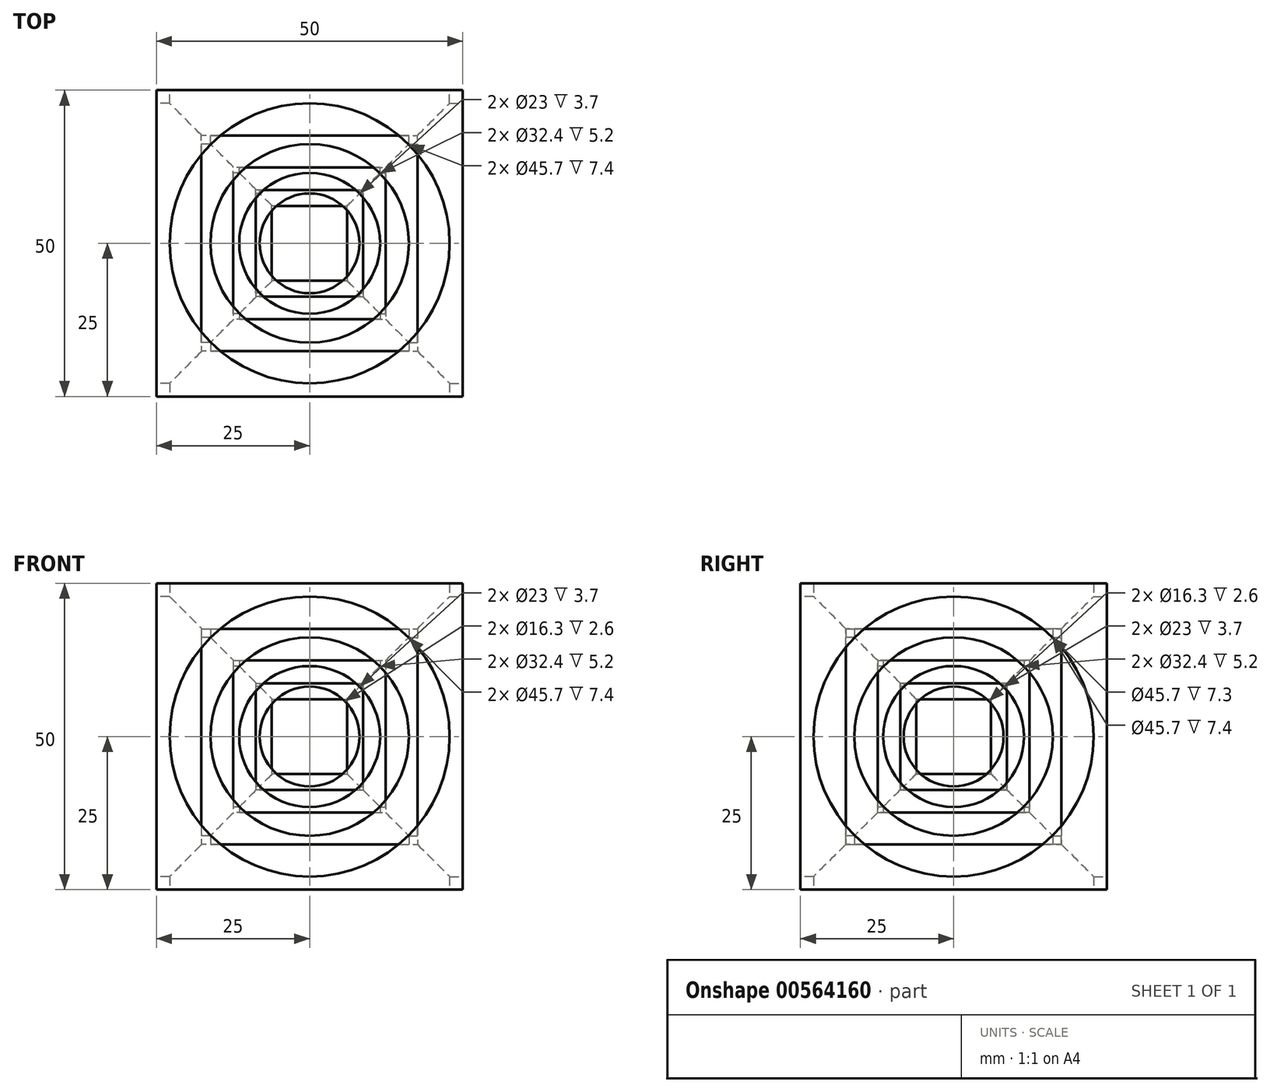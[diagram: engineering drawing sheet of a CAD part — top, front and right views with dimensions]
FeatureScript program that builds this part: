
annotation { "Feature Type Name" : "Feature", "Feature Type Description" : "" }
export const myFeature = defineFeature(function(context is Context, id is Id, definition is map)
    precondition{}
    {
        {
            assignVariable(context, id + "F0", {"name" : "S0", "anyValue" : 50});
        }
        {
            var Q0;
            Q0=qCreatedBy(makeId("Front.planeOp"),FACE);
            var sketch = newSketch(context, id + "F1", { "sketchPlane" : qUnion([Q0])});
            skLineSegment(sketch, "E0", {"start": v(0, 0) * mm, "end": v(-25, 0) * mm, "construction": true});
            skLineSegment(sketch, "E1", {"start": v(-25, 0) * mm, "end": v(-25, 25) * mm});
            skLineSegment(sketch, "E2", {"start": v(-25, 25) * mm, "end": v(25, 25) * mm});
            skLineSegment(sketch, "E3", {"start": v(-25, 0) * mm, "end": v(-25, -25) * mm});
            skLineSegment(sketch, "E4", {"start": v(-25, -25) * mm, "end": v(25, -25) * mm});
            skLineSegment(sketch, "E5", {"start": v(25, -25) * mm, "end": v(25, 25) * mm});
            skSolve(sketch);
        }
        {
            var Q0;
            Q0 = qSketchRegion(id + "F1", true);
            extrude(context, id + "F2", {"entities" : qUnion([Q0]), "depth" : getVariable(context, 'S0') * mm, "offsetDistance" : 25 * mm, "symmetric" : true});
        }
        {
            var Q0;
            Q0=qCreatedBy(makeId("Front.planeOp"),FACE);
            var sketch = newSketch(context, id + "F3", { "sketchPlane" : qUnion([Q0])});
            skLineSegment(sketch, "E6.0.0", {"start": v(-25, -25) * mm, "end": v(25, -25) * mm, "construction": true});
            skLineSegment(sketch, "E6.0.1", {"start": v(25, -25) * mm, "end": v(25, 25) * mm, "construction": true});
            skLineSegment(sketch, "E6.0.2", {"start": v(25, 25) * mm, "end": v(-25, 25) * mm, "construction": true});
            skLineSegment(sketch, "E6.0.3", {"start": v(-25, 25) * mm, "end": v(-25, -25) * mm, "construction": true});
            skLineSegment(sketch, "E7", {"start": v(0, 25) * mm, "end": v(0, 17.6) * mm, "construction": true});
            skPoint(sketch, "E7.endSnap0", {"position": v(0, 25) * mm});
            skLineSegment(sketch, "E8", {"start": v(0, 17.6) * mm, "end": v(0, 12.4) * mm, "construction": true});
            skLineSegment(sketch, "E9", {"start": v(0, 12.4) * mm, "end": v(0, 8.7) * mm, "construction": true});
            skLineSegment(sketch, "E10", {"start": v(0, 8.7) * mm, "end": v(0, 6.1) * mm, "construction": true});
            skLineSegment(sketch, "E11", {"start": v(0, 17.6) * mm, "end": v(22.85, 17.6) * mm, "construction": true});
            skLineSegment(sketch, "E12", {"start": v(0, 12.4) * mm, "end": v(16.2, 12.4) * mm, "construction": true});
            skLineSegment(sketch, "E13", {"start": v(0, 8.7) * mm, "end": v(11.5, 8.7) * mm, "construction": true});
            skLineSegment(sketch, "E14", {"start": v(0, 6.1) * mm, "end": v(8.15, 6.1) * mm, "construction": true});
            skLineSegment(sketch, "E15", {"start": v(0, 25) * mm, "end": v(22.85, 25) * mm});
            skLineSegment(sketch, "E16", {"start": v(22.85, 25) * mm, "end": v(22.85, 17.6) * mm});
            skLineSegment(sketch, "E17", {"start": v(22.85, 17.6) * mm, "end": v(16.2, 17.6) * mm});
            skLineSegment(sketch, "E18", {"start": v(16.2, 17.6) * mm, "end": v(16.2, 12.4) * mm});
            skLineSegment(sketch, "E19", {"start": v(16.2, 12.4) * mm, "end": v(11.5, 12.4) * mm});
            skLineSegment(sketch, "E20", {"start": v(11.5, 12.4) * mm, "end": v(11.5, 8.7) * mm});
            skLineSegment(sketch, "E21", {"start": v(8.15, 8.7) * mm, "end": v(11.5, 8.7) * mm});
            skLineSegment(sketch, "E22", {"start": v(8.15, 8.7) * mm, "end": v(8.15, 6.1) * mm});
            skLineSegment(sketch, "E23", {"start": v(0, 6.1) * mm, "end": v(0, 25) * mm});
            skLineSegment(sketch, "E24", {"start": v(8.15, 6.1) * mm, "end": v(0, 6.1) * mm});
            skSolve(sketch);
        }
        {
            var Q0;
            Q0 = qSketchRegion(id + "F3", true);
            var Q1;
            Q1=sQuery(id+"F3.wireOp",EDGE,"E23");
            revolve(context, id + "F4", {"operationType" : NewBodyOperationType.REMOVE, "entities" : qUnion([Q0]), "axis" : qUnion([Q1]), "revolveType" : RevolveType.FULL});
        }
        {
            var Q0;
            Q0=qCreatedBy(makeId("Front.planeOp"),FACE);
            var sketch = newSketch(context, id + "F5", { "sketchPlane" : qUnion([Q0])});
            skPoint(sketch, "E25.0", {"position": v(25, 25) * mm});
            skPoint(sketch, "E26.0", {"position": v(-25, 25) * mm});
            skPoint(sketch, "E27.0", {"position": v(-25, -25) * mm});
            skPoint(sketch, "E28.0", {"position": v(25, -25) * mm});
            skLineSegment(sketch, "E29.0.0", {"start": v(25, 25) * mm, "end": v(-25, 25) * mm, "construction": true});
            skLineSegment(sketch, "E29.0.1", {"start": v(-25, 25) * mm, "end": v(-25, -25) * mm, "construction": true});
            skLineSegment(sketch, "E29.0.2", {"start": v(-25, -25) * mm, "end": v(25, -25) * mm, "construction": true});
            skLineSegment(sketch, "E29.0.3", {"start": v(25, -25) * mm, "end": v(25, 25) * mm, "construction": true});
            skLineSegment(sketch, "E30", {"start": v(0, -25) * mm, "end": v(0, -17.6) * mm, "construction": true});
            skPoint(sketch, "E30.endSnap0", {"position": v(0, -25) * mm});
            skLineSegment(sketch, "E31", {"start": v(0, -17.6) * mm, "end": v(0, -12.4) * mm, "construction": true});
            skLineSegment(sketch, "E32", {"start": v(0, -12.4) * mm, "end": v(0, -8.7) * mm, "construction": true});
            skLineSegment(sketch, "E33", {"start": v(0, -8.7) * mm, "end": v(0, -6.1) * mm, "construction": true});
            skLineSegment(sketch, "E34", {"start": v(0, -17.6) * mm, "end": v(-22.85, -17.6) * mm, "construction": true});
            skLineSegment(sketch, "E35", {"start": v(0, -12.4) * mm, "end": v(-16.2, -12.4) * mm, "construction": true});
            skLineSegment(sketch, "E36", {"start": v(0, -8.7) * mm, "end": v(-11.5, -8.7) * mm, "construction": true});
            skLineSegment(sketch, "E37", {"start": v(0, -6.1) * mm, "end": v(-8.15, -6.1) * mm, "construction": true});
            skLineSegment(sketch, "E38", {"start": v(0, -25) * mm, "end": v(-22.85, -25) * mm});
            skLineSegment(sketch, "E39", {"start": v(-22.85, -25) * mm, "end": v(-22.85, -17.6) * mm});
            skLineSegment(sketch, "E40", {"start": v(-22.85, -17.6) * mm, "end": v(-16.2, -17.6) * mm});
            skLineSegment(sketch, "E41", {"start": v(-16.2, -17.6) * mm, "end": v(-16.2, -12.4) * mm});
            skLineSegment(sketch, "E42", {"start": v(-16.2, -12.4) * mm, "end": v(-11.5, -12.4) * mm});
            skLineSegment(sketch, "E43", {"start": v(-11.5, -12.4) * mm, "end": v(-11.5, -8.7) * mm});
            skLineSegment(sketch, "E44", {"start": v(-8.15, -8.7) * mm, "end": v(-11.5, -8.7) * mm});
            skLineSegment(sketch, "E45", {"start": v(-8.15, -8.7) * mm, "end": v(-8.15, -6.1) * mm});
            skLineSegment(sketch, "E46", {"start": v(0, -6.1) * mm, "end": v(0, -25) * mm});
            skLineSegment(sketch, "E47", {"start": v(-8.15, -6.1) * mm, "end": v(0, -6.1) * mm});
            skSolve(sketch);
        }
        {
            var Q0;
            Q0 = qSketchRegion(id + "F5", true);
            var Q1;
            Q1=sQuery(id+"F5.wireOp",EDGE,"E46");
            revolve(context, id + "F6", {"operationType" : NewBodyOperationType.REMOVE, "entities" : qUnion([Q0]), "axis" : qUnion([Q1]), "revolveType" : RevolveType.FULL, "oppositeDirection" : true});
        }
        {
            var Q0;
            Q0=qCreatedBy(makeId("Right.planeOp"),FACE);
            var sketch = newSketch(context, id + "F7", { "sketchPlane" : qUnion([Q0])});
            skPoint(sketch, "E48.0", {"position": v(-25, 25) * mm});
            skPoint(sketch, "E49.0", {"position": v(25, -25) * mm});
            skPoint(sketch, "E50.0", {"position": v(25, 25) * mm});
            skPoint(sketch, "E51.0", {"position": v(-25, -25) * mm});
            skLineSegment(sketch, "E52.0.0", {"start": v(25, -25) * mm, "end": v(25, 25) * mm, "construction": true});
            skLineSegment(sketch, "E52.0.1", {"start": v(25, 25) * mm, "end": v(-25, 25) * mm, "construction": true});
            skLineSegment(sketch, "E52.0.2", {"start": v(-25, 25) * mm, "end": v(-25, -25) * mm, "construction": true});
            skLineSegment(sketch, "E52.0.3", {"start": v(-25, -25) * mm, "end": v(25, -25) * mm, "construction": true});
            skLineSegment(sketch, "E53", {"start": v(-25, 0) * mm, "end": v(-17.6, 0) * mm, "construction": true});
            skPoint(sketch, "E53.endSnap0", {"position": v(-25, 0) * mm});
            skLineSegment(sketch, "E54", {"start": v(-17.6, 0) * mm, "end": v(-12.4, 0) * mm, "construction": true});
            skLineSegment(sketch, "E55", {"start": v(-12.4, 0) * mm, "end": v(-8.7, 0) * mm, "construction": true});
            skLineSegment(sketch, "E56", {"start": v(-8.7, 0) * mm, "end": v(-6.1, 0) * mm, "construction": true});
            skLineSegment(sketch, "E57", {"start": v(-17.6, 0) * mm, "end": v(-17.6, 22.85) * mm, "construction": true});
            skLineSegment(sketch, "E58", {"start": v(-12.4, 0) * mm, "end": v(-12.4, 16.2) * mm, "construction": true});
            skLineSegment(sketch, "E59", {"start": v(-8.7, 0) * mm, "end": v(-8.7, 11.5) * mm, "construction": true});
            skLineSegment(sketch, "E60", {"start": v(-6.1, 0) * mm, "end": v(-6.1, 8.15) * mm, "construction": true});
            skLineSegment(sketch, "E61", {"start": v(-25, 0) * mm, "end": v(-25, 22.85) * mm});
            skLineSegment(sketch, "E62", {"start": v(-25, 22.85) * mm, "end": v(-17.6, 22.85) * mm});
            skLineSegment(sketch, "E63", {"start": v(-17.6, 22.85) * mm, "end": v(-17.6, 16.2) * mm});
            skLineSegment(sketch, "E64", {"start": v(-17.6, 16.2) * mm, "end": v(-12.4, 16.2) * mm});
            skLineSegment(sketch, "E65", {"start": v(-12.4, 16.2) * mm, "end": v(-12.4, 11.5) * mm});
            skLineSegment(sketch, "E66", {"start": v(-12.4, 11.5) * mm, "end": v(-8.7, 11.5) * mm});
            skLineSegment(sketch, "E67", {"start": v(-8.7, 8.15) * mm, "end": v(-8.7, 11.5) * mm});
            skLineSegment(sketch, "E68", {"start": v(-8.7, 8.15) * mm, "end": v(-6.1, 8.15) * mm});
            skLineSegment(sketch, "E69", {"start": v(-6.1, 0) * mm, "end": v(-25, 0) * mm});
            skLineSegment(sketch, "E70", {"start": v(-6.1, 8.15) * mm, "end": v(-6.1, 0) * mm});
            skSolve(sketch);
        }
        {
            var Q0;
            Q0 = qSketchRegion(id + "F7", true);
            var Q1;
            Q1=sQuery(id+"F7.wireOp",EDGE,"E69");
            revolve(context, id + "F8", {"operationType" : NewBodyOperationType.REMOVE, "entities" : qUnion([Q0]), "axis" : qUnion([Q1]), "revolveType" : RevolveType.FULL, "oppositeDirection" : true});
        }
        {
            var Q0;
            Q0=qCreatedBy(makeId("Right.planeOp"),FACE);
            var sketch = newSketch(context, id + "F9", { "sketchPlane" : qUnion([Q0])});
            skPoint(sketch, "E71.0", {"position": v(-25, -25) * mm});
            skPoint(sketch, "E72.0", {"position": v(-25, 25) * mm});
            skPoint(sketch, "E73.0", {"position": v(25, 25) * mm});
            skPoint(sketch, "E74.0", {"position": v(25, -25) * mm});
            skLineSegment(sketch, "E75.0.0", {"start": v(-25, 25) * mm, "end": v(-25, -25) * mm, "construction": true});
            skLineSegment(sketch, "E75.0.1", {"start": v(-25, -25) * mm, "end": v(25, -25) * mm, "construction": true});
            skLineSegment(sketch, "E75.0.2", {"start": v(25, -25) * mm, "end": v(25, 25) * mm, "construction": true});
            skLineSegment(sketch, "E75.0.3", {"start": v(25, 25) * mm, "end": v(-25, 25) * mm, "construction": true});
            skLineSegment(sketch, "E76", {"start": v(25, 0) * mm, "end": v(17.6, 0) * mm, "construction": true});
            skPoint(sketch, "E76.endSnap0", {"position": v(25, 0) * mm});
            skLineSegment(sketch, "E77", {"start": v(17.6, 0) * mm, "end": v(12.4, 0) * mm, "construction": true});
            skLineSegment(sketch, "E78", {"start": v(12.4, 0) * mm, "end": v(8.7, 0) * mm, "construction": true});
            skLineSegment(sketch, "E79", {"start": v(8.7, 0) * mm, "end": v(6.1, 0) * mm, "construction": true});
            skLineSegment(sketch, "E80", {"start": v(17.6, 0) * mm, "end": v(17.6, -22.85) * mm, "construction": true});
            skLineSegment(sketch, "E81", {"start": v(12.4, 0) * mm, "end": v(12.4, -16.2) * mm, "construction": true});
            skLineSegment(sketch, "E82", {"start": v(8.7, 0) * mm, "end": v(8.7, -11.5) * mm, "construction": true});
            skLineSegment(sketch, "E83", {"start": v(6.1, 0) * mm, "end": v(6.1, -8.15) * mm, "construction": true});
            skLineSegment(sketch, "E84", {"start": v(25, 0) * mm, "end": v(25, -22.85) * mm});
            skLineSegment(sketch, "E85", {"start": v(25, -22.85) * mm, "end": v(17.6, -22.85) * mm});
            skLineSegment(sketch, "E86", {"start": v(17.6, -22.85) * mm, "end": v(17.6, -16.2) * mm});
            skLineSegment(sketch, "E87", {"start": v(17.6, -16.2) * mm, "end": v(12.4, -16.2) * mm});
            skLineSegment(sketch, "E88", {"start": v(12.4, -16.2) * mm, "end": v(12.4, -11.5) * mm});
            skLineSegment(sketch, "E89", {"start": v(12.4, -11.5) * mm, "end": v(8.7, -11.5) * mm});
            skLineSegment(sketch, "E90", {"start": v(8.7, -8.15) * mm, "end": v(8.7, -11.5) * mm});
            skLineSegment(sketch, "E91", {"start": v(8.7, -8.15) * mm, "end": v(6.1, -8.15) * mm});
            skLineSegment(sketch, "E92", {"start": v(6.1, 0) * mm, "end": v(25, 0) * mm});
            skLineSegment(sketch, "E93", {"start": v(6.1, -8.15) * mm, "end": v(6.1, 0) * mm});
            skSolve(sketch);
        }
        {
            var Q0;
            Q0=makeQuery(id+"F9.imprint","IMPRINT",FACE,{"disambiguationData":[TD([[makeQuery(id+"F9.imprint","IMPRINT",EDGE,{"derivedFrom":sQuery(id+"F9.wireOp",EDGE,"E84")}),-1.0]])]});
            var Q1;
            Q1=sQuery(id+"F9.wireOp",EDGE,"E92");
            revolve(context, id + "F10", {"operationType" : NewBodyOperationType.REMOVE, "entities" : qUnion([Q0]), "axis" : qUnion([Q1]), "revolveType" : RevolveType.FULL, "oppositeDirection" : true});
        }
        {
            var Q0;
            Q0=qCreatedBy(makeId("Front.planeOp"),FACE);
            var sketch = newSketch(context, id + "F11", { "sketchPlane" : qUnion([Q0])});
            skPoint(sketch, "E94.0", {"position": v(25, -25) * mm});
            skPoint(sketch, "E95.0", {"position": v(-25, -25) * mm});
            skPoint(sketch, "E96.0", {"position": v(-25, 25) * mm});
            skPoint(sketch, "E97.0", {"position": v(25, 25) * mm});
            skPoint(sketch, "E98.0", {"position": v(-25.1, 25) * mm});
            skPoint(sketch, "E99.0", {"position": v(24.9, -25) * mm});
            skPoint(sketch, "E100.0", {"position": v(24.9, 25) * mm});
            skPoint(sketch, "E101.0", {"position": v(-25.1, -25) * mm});
            skLineSegment(sketch, "E102.0.0", {"start": v(24.9, -25) * mm, "end": v(24.9, 25) * mm, "construction": true});
            skLineSegment(sketch, "E102.0.1", {"start": v(24.9, 25) * mm, "end": v(-25.1, 25) * mm, "construction": true});
            skLineSegment(sketch, "E102.0.2", {"start": v(-25.1, 25) * mm, "end": v(-25.1, -25) * mm, "construction": true});
            skLineSegment(sketch, "E102.0.3", {"start": v(-25.1, -25) * mm, "end": v(24.9, -25) * mm, "construction": true});
            skLineSegment(sketch, "E103", {"start": v(-25.1, 0) * mm, "end": v(-17.7, 0) * mm, "construction": true});
            skPoint(sketch, "E103.endSnap0", {"position": v(-25.1, 0) * mm});
            skLineSegment(sketch, "E104", {"start": v(-17.7, 0) * mm, "end": v(-12.5, 0) * mm, "construction": true});
            skLineSegment(sketch, "E105", {"start": v(-12.5, 0) * mm, "end": v(-8.8, 0) * mm, "construction": true});
            skLineSegment(sketch, "E106", {"start": v(-8.8, 0) * mm, "end": v(-6.2, 0) * mm, "construction": true});
            skLineSegment(sketch, "E107", {"start": v(-17.7, 0) * mm, "end": v(-17.7, 22.85) * mm, "construction": true});
            skLineSegment(sketch, "E108", {"start": v(-12.5, 0) * mm, "end": v(-12.5, 16.2) * mm, "construction": true});
            skLineSegment(sketch, "E109", {"start": v(-8.8, 0) * mm, "end": v(-8.8, 11.5) * mm, "construction": true});
            skLineSegment(sketch, "E110", {"start": v(-6.2, 0) * mm, "end": v(-6.2, 8.15) * mm, "construction": true});
            skLineSegment(sketch, "E111", {"start": v(-25.1, 0) * mm, "end": v(-25.1, 22.85) * mm});
            skLineSegment(sketch, "E112", {"start": v(-25.1, 22.85) * mm, "end": v(-17.7, 22.85) * mm});
            skLineSegment(sketch, "E113", {"start": v(-17.7, 22.85) * mm, "end": v(-17.7, 16.2) * mm});
            skLineSegment(sketch, "E114", {"start": v(-17.7, 16.2) * mm, "end": v(-12.5, 16.2) * mm});
            skLineSegment(sketch, "E115", {"start": v(-12.5, 16.2) * mm, "end": v(-12.5, 11.5) * mm});
            skLineSegment(sketch, "E116", {"start": v(-12.5, 11.5) * mm, "end": v(-8.8, 11.5) * mm});
            skLineSegment(sketch, "E117", {"start": v(-8.8, 8.15) * mm, "end": v(-8.8, 11.5) * mm});
            skLineSegment(sketch, "E118", {"start": v(-8.8, 8.15) * mm, "end": v(-6.2, 8.15) * mm});
            skLineSegment(sketch, "E119", {"start": v(-6.2, 0) * mm, "end": v(-25.1, 0) * mm});
            skLineSegment(sketch, "E120", {"start": v(-6.2, 8.15) * mm, "end": v(-6.2, 0) * mm});
            skSolve(sketch);
        }
        {
            var Q0;
            Q0 = qSketchRegion(id + "F11", true);
            var Q1;
            Q1=sQuery(id+"F11.wireOp",EDGE,"E119");
            revolve(context, id + "F12", {"operationType" : NewBodyOperationType.REMOVE, "entities" : qUnion([Q0]), "axis" : qUnion([Q1]), "revolveType" : RevolveType.FULL, "oppositeDirection" : true});
        }
        {
            var Q0;
            Q0=qCreatedBy(makeId("Front.planeOp"),FACE);
            var sketch = newSketch(context, id + "F13", { "sketchPlane" : qUnion([Q0])});
            skPoint(sketch, "E121.0", {"position": v(25, -25) * mm});
            skPoint(sketch, "E122.0", {"position": v(-25, -25) * mm});
            skPoint(sketch, "E123.0", {"position": v(-25, 25) * mm});
            skPoint(sketch, "E124.0", {"position": v(25, 25) * mm});
            skLineSegment(sketch, "E125.0.0", {"start": v(-25, 25) * mm, "end": v(-25, -25) * mm, "construction": true});
            skLineSegment(sketch, "E125.0.1", {"start": v(-25, -25) * mm, "end": v(25, -25) * mm, "construction": true});
            skLineSegment(sketch, "E125.0.2", {"start": v(25, -25) * mm, "end": v(25, 25) * mm, "construction": true});
            skLineSegment(sketch, "E125.0.3", {"start": v(25, 25) * mm, "end": v(-25, 25) * mm, "construction": true});
            skLineSegment(sketch, "E126", {"start": v(25, 0) * mm, "end": v(17.6, 0) * mm, "construction": true});
            skPoint(sketch, "E126.endSnap0", {"position": v(25, 0) * mm});
            skLineSegment(sketch, "E127", {"start": v(17.6, 0) * mm, "end": v(12.4, 0) * mm, "construction": true});
            skLineSegment(sketch, "E128", {"start": v(12.4, 0) * mm, "end": v(8.7, 0) * mm, "construction": true});
            skLineSegment(sketch, "E129", {"start": v(8.7, 0) * mm, "end": v(6.1, 0) * mm, "construction": true});
            skLineSegment(sketch, "E130", {"start": v(17.6, 0) * mm, "end": v(17.6, -22.85) * mm, "construction": true});
            skLineSegment(sketch, "E131", {"start": v(12.4, 0) * mm, "end": v(12.4, -16.2) * mm, "construction": true});
            skLineSegment(sketch, "E132", {"start": v(8.7, 0) * mm, "end": v(8.7, -11.5) * mm, "construction": true});
            skLineSegment(sketch, "E133", {"start": v(6.1, 0) * mm, "end": v(6.1, -8.15) * mm, "construction": true});
            skLineSegment(sketch, "E134", {"start": v(25, 0) * mm, "end": v(25, -22.85) * mm});
            skLineSegment(sketch, "E135", {"start": v(25, -22.85) * mm, "end": v(17.6, -22.85) * mm});
            skLineSegment(sketch, "E136", {"start": v(17.6, -22.85) * mm, "end": v(17.6, -16.2) * mm});
            skLineSegment(sketch, "E137", {"start": v(17.6, -16.2) * mm, "end": v(12.4, -16.2) * mm});
            skLineSegment(sketch, "E138", {"start": v(12.4, -16.2) * mm, "end": v(12.4, -11.5) * mm});
            skLineSegment(sketch, "E139", {"start": v(12.4, -11.5) * mm, "end": v(8.7, -11.5) * mm});
            skLineSegment(sketch, "E140", {"start": v(8.7, -8.15) * mm, "end": v(8.7, -11.5) * mm});
            skLineSegment(sketch, "E141", {"start": v(8.7, -8.15) * mm, "end": v(6.1, -8.15) * mm});
            skLineSegment(sketch, "E142", {"start": v(6.1, 0) * mm, "end": v(25, 0) * mm});
            skLineSegment(sketch, "E143", {"start": v(6.1, -8.15) * mm, "end": v(6.1, 0) * mm});
            skSolve(sketch);
        }
        {
            var Q0;
            Q0 = qSketchRegion(id + "F13", true);
            var Q1;
            Q1=sQuery(id+"F13.wireOp",EDGE,"E142");
            revolve(context, id + "F14", {"operationType" : NewBodyOperationType.REMOVE, "entities" : qUnion([Q0]), "axis" : qUnion([Q1]), "revolveType" : RevolveType.FULL, "oppositeDirection" : true});
        }
    });
